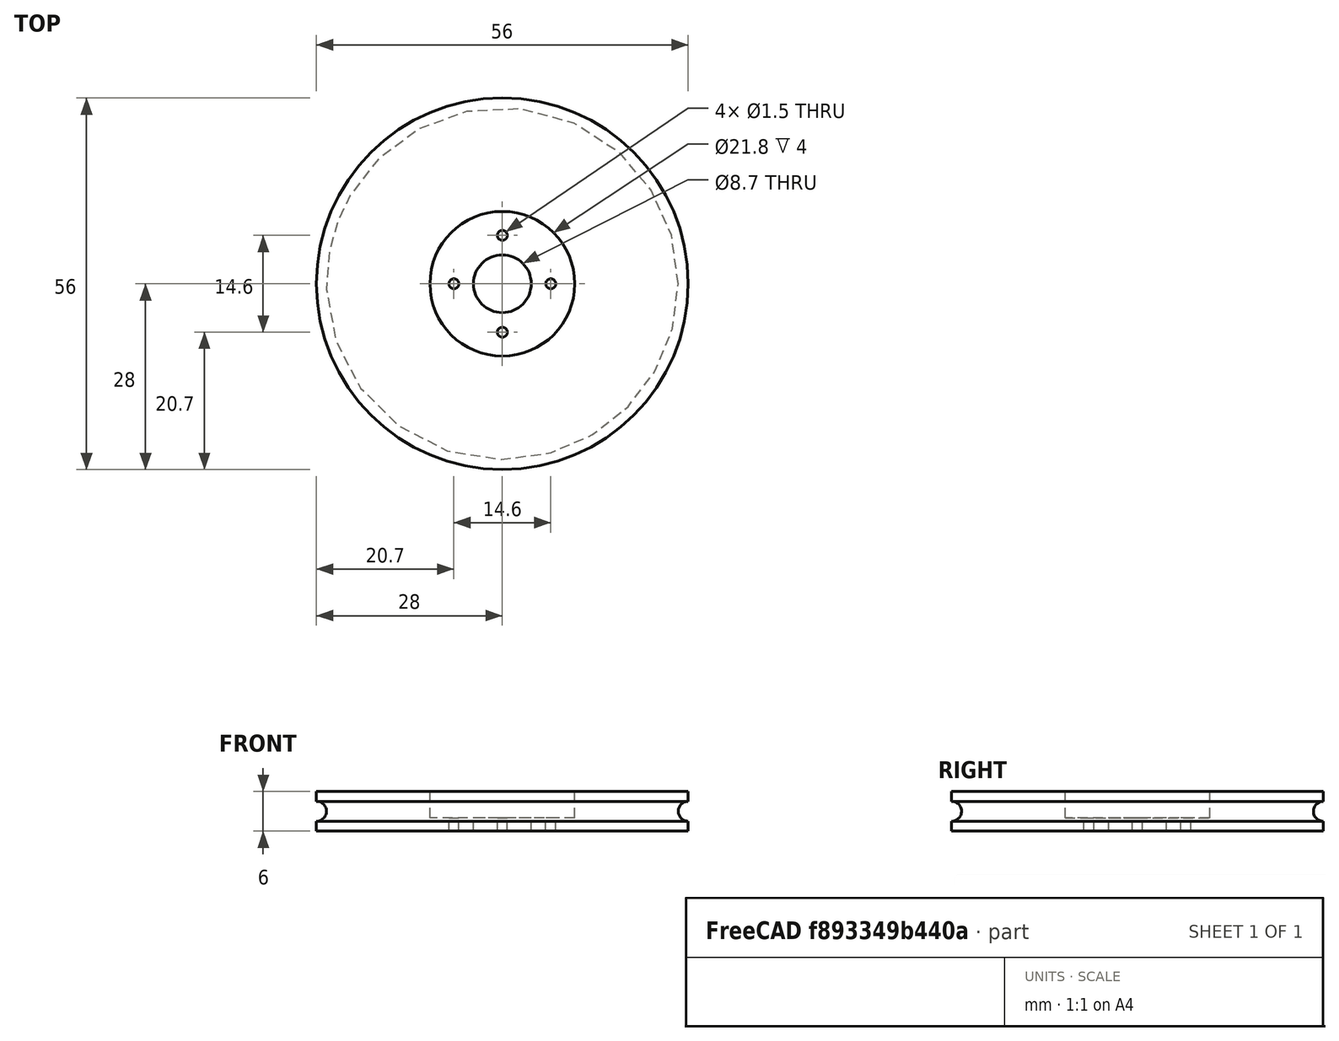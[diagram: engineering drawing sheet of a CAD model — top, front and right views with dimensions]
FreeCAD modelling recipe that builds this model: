
FCSTD DOCUMENT  (FreeCAD 0.16R6707 (Git))
Label: Rueda_MiniSkybot
License: CreativeCommons Attribution-ShareAlike
LicenseURL: http://creativecommons.org/licenses/by-sa/4.0/
objects: Part::Cylinder×4, Part::Cut×4, Part::Torus×1, Part::FeaturePython×1
note: 10 computed .brp shape members not serialized (recipe doc carries the construction recipe); baked Part::Feature solids carry a one-line shape summary decoded from their .brp

FEATURE [Part::Cylinder] Cylinder  label="Rueda_base"
  Angle = 360
  Height = 6
  Radius = 28
FEATURE [Part::Torus] Torus  label="Vaciaod_junta_torica"
  Angle1 = -180
  Angle2 = 180
  Angle3 = 360
  Placement = pos=(0,0,3) rot=(0,0,1;0rad)
  Radius1 = 28
  Radius2 = 1.5
FEATURE [Part::Cut] Cut  label="Rueda_basica"
  Base = -> Cylinder
  Tool = -> Torus
FEATURE [Part::Cylinder] Cylinder001  label="Corona_servo"
  Angle = 360
  Height = 10
  Placement = pos=(0,0,2) rot=(0,0,1;0rad)
  Radius = 10.9
FEATURE [Part::Cut] Cut001  label="Rueda_con_hueco_corona"
  Base = -> Cut
  Tool = -> Cylinder001
FEATURE [Part::Cylinder] Cylinder002  label="Hueco_eje"
  Angle = 360
  Height = 10
  Placement = pos=(0,0,-2) rot=(0,0,1;0rad)
  Radius = 4.35
FEATURE [Part::Cut] Cut002  label="Rueda_corona_eje"
  Base = -> Cut001
  Tool = -> Cylinder002
FEATURE [Part::Cylinder] Cylinder003  label="Taladro"
  Angle = 360
  Height = 10
  Placement = pos=(7.3,0,-2) rot=(0,0,1;0rad)
  Radius = 0.75
FEATURE [Part::FeaturePython] Array  # Draft array (typed FeaturePython)
  Angle = 360
  ArrayType = 1
  Axis = (0,0,1)
  Base = -> Cylinder003
  Center = (0,0,0)
  Fuse = false
  IntervalAxis = (0,0,0)
  IntervalX = (1,0,0)
  IntervalY = (0,1,0)
  IntervalZ = (0,0,0)
  NumberPolar = 4
  NumberX = 2
  NumberY = 2
  NumberZ = 1
FEATURE [Part::Cut] Cut003  label="Rueda_miniskybot"
  Base = -> Cut002
  Tool = -> Array
